# Revit family: Plumbing_Drainage_hansgrohe_01000XXX-uBox-universal-Base-set-for-fin_NEW
name_source: partatom
category: Plumbing Fixtures
revit_build: Autodesk Revit 2018 (Build: 20170223_1515(x64)
units: mm (PartAtom-declared; Revit-internal decimal feet)

## family parameters
Cut with Voids When Loaded = Yes
Host = Face
OmniClass Number = 23.31.17.29
OmniClass Title = Shower Drains
Part Type = Normal
Room Calculation Point = No
Round Connector Dimension = Use Diameter
Shared = No

## types (1)
- 01000XXX uBox universal Base set for finish sets for flat installation
    BIMobject category = Drainage
    Connector Description = Water Outlet 48 mm
    Default Elevation = 0 mm  [stored 0 ft]
    Description = uBox universal Base set for finish sets for flat installation
    Design country = Germany
    Diameter = 48  [stored 0.15748 ft]
    Edition number = 1
    IFC Classification = Pipe Fitting
    Manufacturer = Hansgrohe
    Manufacturer country = Germany
    Manufacturer name = hansgrohe
    Material 1 = Hansgrohe - Plastic - Dark Gray
    Material 2 = Hansgrohe - Plastic - Gray
    Model = 01000XXX
    OmniClass Code = 23-31 17 29
    OmniClass Description = Shower Drains
    Product Guid = df4c71ec-1ad6-4edd-b526-ba07d2dd4357
    Product SKU = 01000XXX
    Product data url = https://bimobject.com
    Product family = uBox universal
    Product group = Concealed basic set shower drains
    Product name = 01000XXX uBox universal Base set for finish sets for flat installation
    Product url = https://www.hansgrohe.com
    QR code = https://bimobject.com
    URL = https://www.hansgrohe.com
    Uniclass 2015 Code = Pr_40_20_96_81
    Uniclass 2015 Name = Sinks
    Weight Net (Kg) = 1.2

note: [stored X ft] marks values corroborated as IEEE doubles in the binary element streams (Revit-internal decimal feet)

## geometry (parser evidence)
native form markers: Sweep x6
no freeform markers — native parametric forms only
